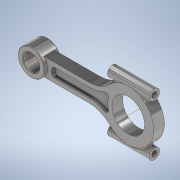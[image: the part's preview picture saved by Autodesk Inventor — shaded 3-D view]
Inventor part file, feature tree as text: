
AUTODESK INVENTOR PART (.ipt)
format: ipt  version: 2021 (Build 250183000, 183)  size: 436,224 bytes
history: native  units: mm
features: other x4, sketch x4, extrude x4, mirror x2, fillet x2, hole x1
ambient origin geometry x8: Origin, YZ Plane, XZ Plane, XY Plane, X Axis, Y Axis, Z Axis, Center Point
bodies: Body1 (feature_tree)
feature tree (17):
  other  "Твердое тело1"
  sketch  "Эскиз1"
  extrude  "Выдавливание1"  Depth=28.0mm
  extrude  "Выдавливание2"  Depth=45.0mm
  extrude  "Выдавливание3"  Depth=159.0mm
  mirror  "Зеркальное отражение1"
  other  "РабПлоскость1"
  extrude  "Выдавливание4"  Depth=55.0mm
  hole  "Отверстие1"  [1 undecoded]
  fillet  "Сопряжение1"  Radius=15.0mm
  mirror  "Зеркальное отражение2"
  fillet  "Сопряжение2"  Radius=50.0mm
  other  "РабОсь1"
  other  "РабОсь2"
  sketch  "Эскиз2"
  sketch  "Эскиз3"
  sketch  "Эскиз4"
note: 1 required parameter value undecoded (feature->parameter linkage not recoverable at this tier; creation-order binding heuristic only, values carry confidence <= 0.55)
